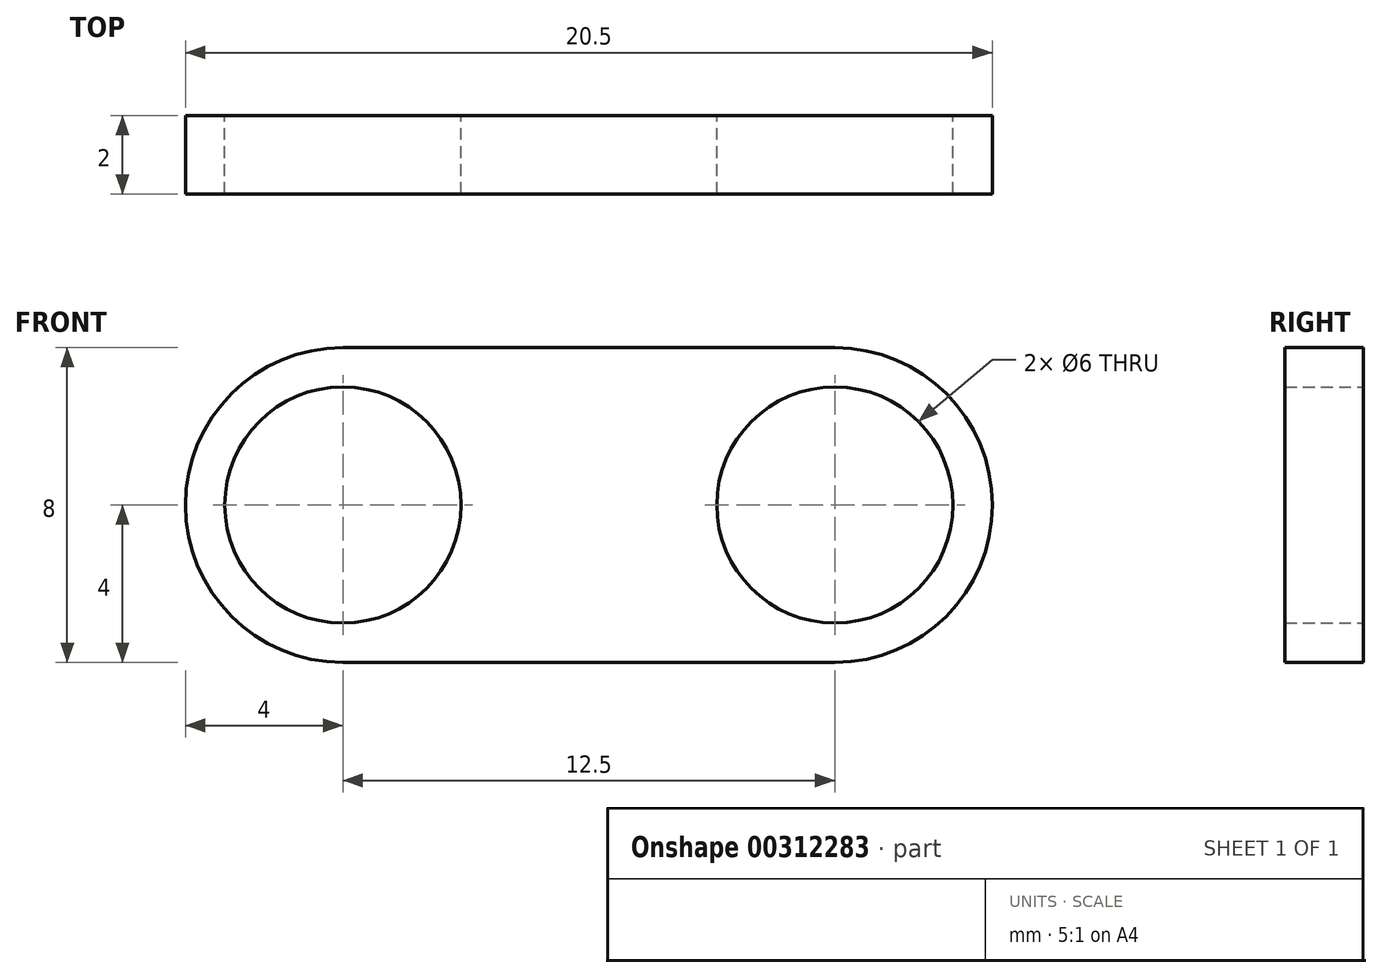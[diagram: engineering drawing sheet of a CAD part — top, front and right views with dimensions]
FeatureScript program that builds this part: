
annotation { "Feature Type Name" : "Feature", "Feature Type Description" : "" }
export const myFeature = defineFeature(function(context is Context, id is Id, definition is map)
    precondition{}
    {
        {
            var Q0;
            Q0=qCreatedBy(makeId("Front.planeOp"),FACE);
            var sketch = newSketch(context, id + "F0", { "sketchPlane" : qUnion([Q0])});
            skCircle(sketch, "E0", {"center": v(-6.25, 0) * mm, "radius": 3 * mm});
            skCircle(sketch, "E1", {"center": v(6.25, 0) * mm, "radius": 3 * mm});
            skArc(sketch, "E2", {"start": v(-6.25, 4) * mm, "mid": v(-10.25, 0) * mm, "end": v(-6.25, -4) * mm});
            skArc(sketch, "E3", {"start": v(6.25, -4) * mm, "mid": v(10.25, 0) * mm, "end": v(6.25, 4) * mm});
            skLineSegment(sketch, "E4", {"start": v(-6.25, 4) * mm, "end": v(6.25, 4) * mm});
            skLineSegment(sketch, "E5", {"start": v(-6.25, -4) * mm, "end": v(6.25, -4) * mm});
            skSolve(sketch);
        }
        {
            var Q0;
            Q0=qSketchRegion(id+"F0",true);
            extrude(context, id + "F1", {"entities" : qUnion([Q0]), "depth" : 2 * mm});
        }
    });
